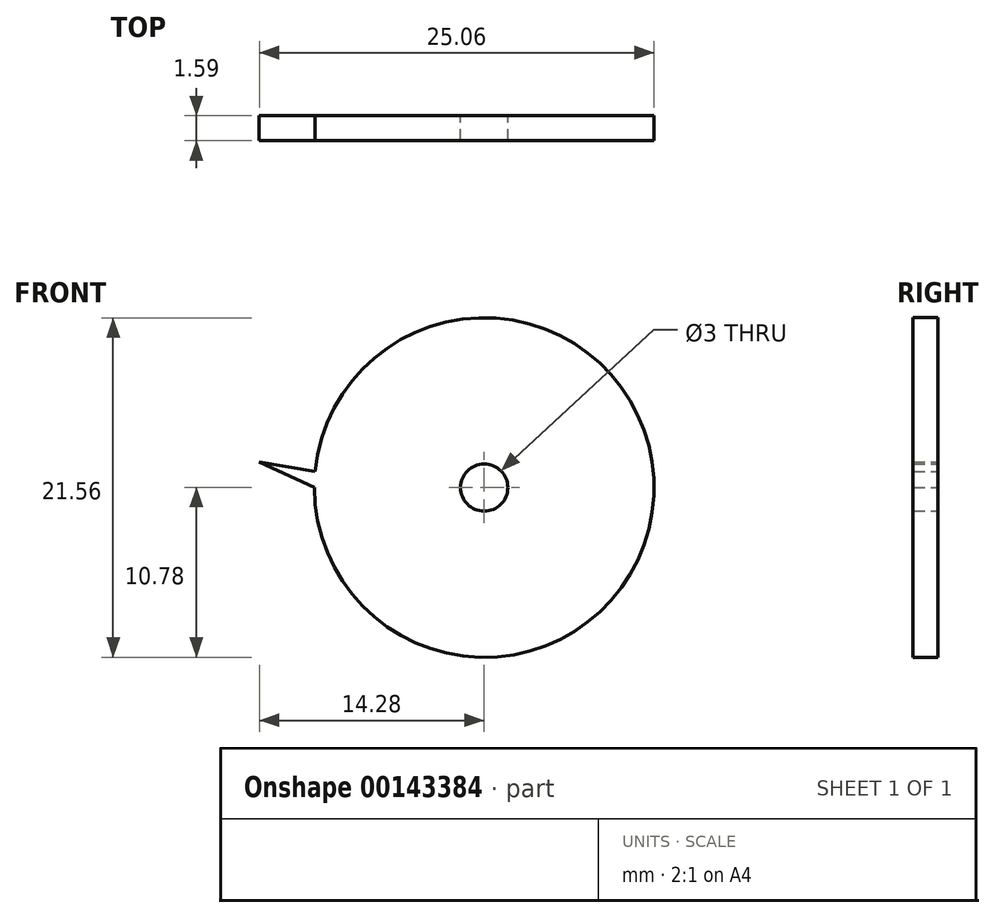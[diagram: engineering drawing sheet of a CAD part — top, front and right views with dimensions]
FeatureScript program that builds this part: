
annotation { "Feature Type Name" : "Feature", "Feature Type Description" : "" }
export const myFeature = defineFeature(function(context is Context, id is Id, definition is map)
    precondition{}
    {
        {
            var Q0;
            Q0=qCreatedBy(makeId("Front.planeOp"),FACE);
            var sketch = newSketch(context, id + "F0", { "sketchPlane" : qUnion([Q0])});
            skCircle(sketch, "E0", {"center": v(0, 0) * mm, "radius": 10.78 * mm});
            skLineSegment(sketch, "E1", {"start": v(-10.78, 0) * mm, "end": v(-14.28, 1.63) * mm});
            skPoint(sketch, "E2.endSnap0", {"position": v(-12.53, 0.82) * mm});
            skLineSegment(sketch, "E3", {"start": v(-14.28, 1.63) * mm, "end": v(-10.74, 1) * mm});
            skCircle(sketch, "E4", {"center": v(0, 0) * mm, "radius": 1.5 * mm});
            skLineSegment(sketch, "E5", {"start": v(-23.85, 0) * mm, "end": v(-3.39, 0) * mm});
            skSolve(sketch);
        }
        {
            var Q0;
            Q0=qSketchRegion(id+"F0",true);
            extrude(context, id + "F1", {"entities" : qUnion([Q0]), "depth" : 1.59 * mm});
        }
        {
            var Q0;
            Q0=qSketchRegion(id+"F0",true);
            extrude(context, id + "F2", {"entities" : qUnion([Q0]), "operationType" : NewBodyOperationType.ADD, "depth" : 1 / 406.4 * mm});
        }
    });
